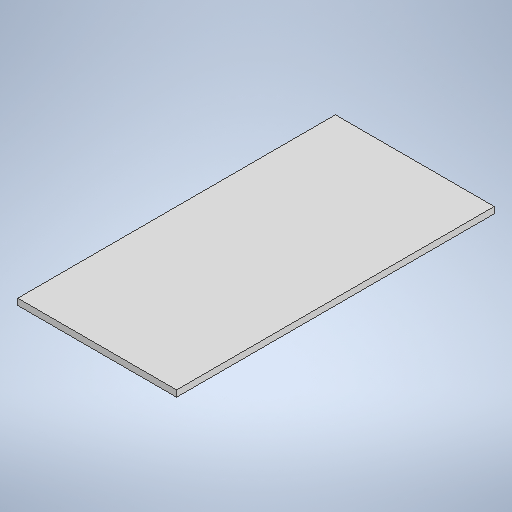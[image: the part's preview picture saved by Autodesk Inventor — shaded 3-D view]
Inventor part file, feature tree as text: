
AUTODESK INVENTOR PART (.ipt)
format: ipt  version: 2025.2 (Build 292293000, 293)  size: 215,040 bytes
history: native  units: mm
features: extrude x1, sketch x1
ambient origin geometry x8: Origin, YZ Plane, XZ Plane, XY Plane, X Axis, Y Axis, Z Axis, Center Point
bodies: Solid1 (feature_tree)
feature tree (2):
  extrude  "Extrusion1"  Depth=500.0mm
  sketch  "Sketch1"  dims[d0=250.0mm d1=500.0mm d2=10.0mm d3=0.0mm]
